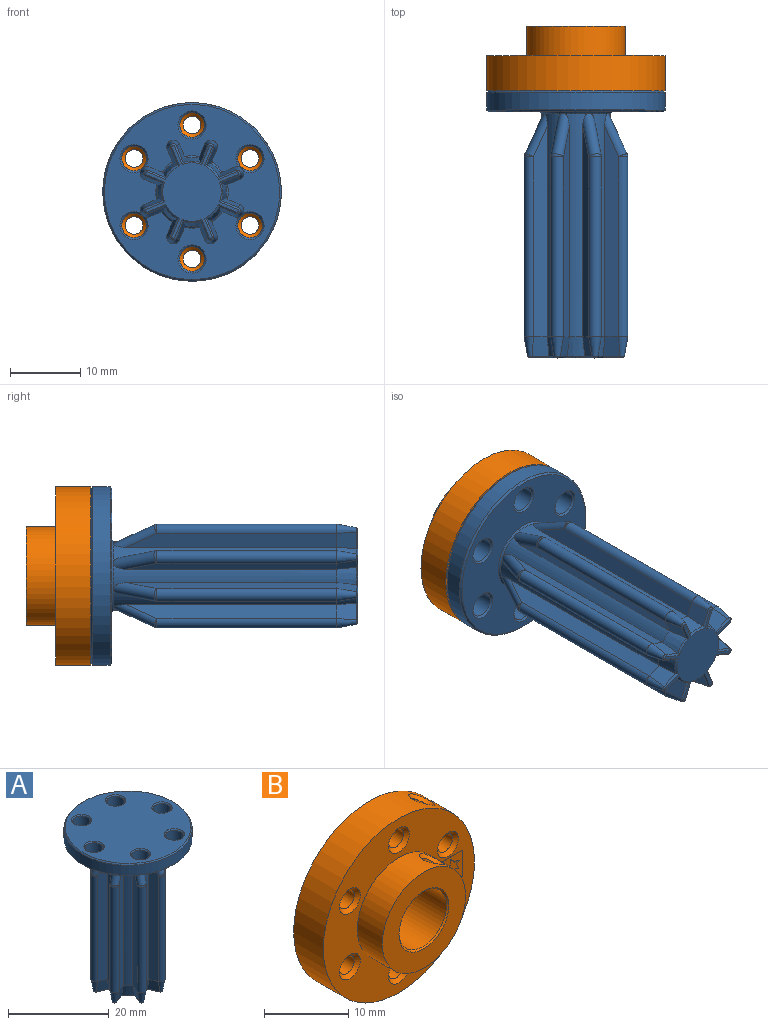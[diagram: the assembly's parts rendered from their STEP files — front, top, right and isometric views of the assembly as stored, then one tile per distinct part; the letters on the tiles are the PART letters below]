
ASSEMBLY  parts=2 mates=1
PART A: 137 faces, bbox 25.4x25.4x38 mm
  f0: cylinder r=4.9mm len=31.75mm, axis (0,0,1), area 62.1mm2, adj f20,f23,f45,f74,f76,f129
  f1: cylinder r=4.9mm len=31.75mm, axis (0,0,1), area 62.1mm2, adj f17,f19,f37,f76,f78,f129
  f2: cylinder r=4.9mm len=31.75mm, axis (0,0,1), area 62.1mm2, adj f14,f16,f36,f78,f81,f129
  f3: cylinder r=4.9mm len=31.75mm, axis (0,0,1), area 62.1mm2, adj f13,f30,f44,f81,f82,f129
  f4: cylinder r=4.9mm len=31.75mm, axis (0,0,1), area 62.1mm2, adj f29,f31,f52,f82,f84,f129
  f5: cylinder r=4.9mm len=31.75mm, axis (0,0,1), area 62.1mm2, adj f25,f28,f60,f84,f86,f129
  f6: cylinder r=4.9mm len=31.75mm, axis (0,0,1), area 62.1mm2, adj f8,f26,f61,f86,f88,f129
  f7: cylinder r=4.9mm len=31.75mm, axis (0,0,1), area 62.1mm2, adj f9,f22,f53,f74,f88,f129
  f8: plane 29.88x1.98mm, normal (0.38,-0.92,0), area 59.4mm2, adj f6,f10,f59,f88
  f9: plane 29.88x1.98mm, normal (-0.38,0.92,0), area 59.4mm2, adj f7,f10,f55,f88
  f10: cylinder r=0.95mm len=25.59mm, axis (0,0,1), area 76.4mm2, adj f8,f9,f57,f89
  f11: plane 13.26x13.26mm, normal (0,0,-1), area 64.4mm2, adj f90,f91,f92,f93,f94,f95,f96,f97
  f12: cylinder r=0.95mm len=25.59mm, axis (0,0,1), area 76.4mm2, adj f13,f14,f40,f80
  f13: plane 29.88x1.98mm, normal (0.38,-0.92,0), area 59.4mm2, adj f3,f12,f42,f81
  f14: plane 29.88x1.98mm, normal (-0.38,0.92,0), area 59.4mm2, adj f2,f12,f38,f81
  f15: cylinder r=0.95mm len=25.59mm, axis (0,0,1), area 76.4mm2, adj f16,f17,f33,f79
  f16: plane 29.88x1.98mm, normal (0.92,-0.38,0), area 59.4mm2, adj f2,f15,f34,f78
  f17: plane 29.88x1.98mm, normal (-0.92,0.38,0), area 59.4mm2, adj f1,f15,f35,f78
  f18: cylinder r=0.95mm len=25.59mm, axis (0,0,1), area 76.4mm2, adj f19,f20,f41,f77
  f19: plane 29.88x1.98mm, normal (0.92,0.38,0), area 59.4mm2, adj f1,f18,f39,f76
  f20: plane 29.88x1.98mm, normal (-0.92,-0.38,0), area 59.4mm2, adj f0,f18,f43,f76
  f21: cylinder r=0.95mm len=25.59mm, axis (0,0,1), area 76.4mm2, adj f22,f23,f49,f75
  f22: plane 29.88x1.98mm, normal (-0.38,-0.92,0), area 59.4mm2, adj f7,f21,f51,f74
  f23: plane 29.88x1.98mm, normal (0.38,0.92,0), area 59.4mm2, adj f0,f21,f47,f74
  f24: cylinder r=0.95mm len=25.59mm, axis (0,0,1), area 76.4mm2, adj f25,f26,f64,f87
  f25: plane 29.88x1.98mm, normal (0.92,-0.38,0), area 59.4mm2, adj f5,f24,f62,f86
  f26: plane 29.88x1.98mm, normal (-0.92,0.38,0), area 59.4mm2, adj f6,f24,f63,f86
  f27: cylinder r=0.95mm len=25.59mm, axis (0,0,1), area 76.4mm2, adj f28,f29,f56,f85
  f28: plane 29.88x1.98mm, normal (-0.92,-0.38,0), area 59.4mm2, adj f5,f27,f58,f84
  f29: plane 29.88x1.98mm, normal (0.92,0.38,0), area 59.4mm2, adj f4,f27,f54,f84
  f30: plane 29.88x1.98mm, normal (0.38,0.92,0), area 59.4mm2, adj f3,f32,f46,f82
  f31: plane 29.88x1.98mm, normal (-0.38,-0.92,0), area 59.4mm2, adj f4,f32,f50,f82
  f32: cylinder r=0.95mm len=25.59mm, axis (0,0,1), area 76.4mm2, adj f30,f31,f48,f83
  f33: cone r=0.42mm half-angle=10deg, axis (0,0,1), area 6.3mm2, adj f15,f34,f35,f110
  f34: plane 2.81x2.39mm, normal (0.91,-0.38,-0.17), area 6.7mm2, adj f16,f33,f36,f108
  f35: plane 2.81x2.58mm, normal (-0.91,0.38,-0.17), area 6.7mm2, adj f17,f33,f37,f112
  f36: cone r=4.37mm half-angle=10deg, axis (0,0,1), area 6.4mm2, adj f2,f34,f38,f106
  f37: cone r=4.37mm half-angle=10deg, axis (0,0,1), area 6.4mm2, adj f1,f35,f39,f114
  f38: plane 2.81x2.39mm, normal (-0.38,0.91,-0.17), area 6.7mm2, adj f14,f36,f40,f104
  f39: plane 2.81x2.58mm, normal (0.91,0.38,-0.17), area 6.7mm2, adj f19,f37,f41,f116
  f40: cone r=0.42mm half-angle=10deg, axis (0,0,1), area 6.3mm2, adj f12,f38,f42,f102
  f41: cone r=0.42mm half-angle=10deg, axis (0,0,1), area 6.3mm2, adj f18,f39,f43,f118
  f42: plane 2.81x2.58mm, normal (0.38,-0.91,-0.17), area 6.7mm2, adj f13,f40,f44,f100
  f43: plane 2.81x2.39mm, normal (-0.91,-0.38,-0.17), area 6.7mm2, adj f20,f41,f45,f120
  f44: cone r=4.37mm half-angle=10deg, axis (0,0,1), area 6.4mm2, adj f3,f42,f46,f98
  f45: cone r=4.37mm half-angle=10deg, axis (0,0,1), area 6.4mm2, adj f0,f43,f47,f121
  f46: plane 2.81x2.58mm, normal (0.38,0.91,-0.17), area 6.7mm2, adj f30,f44,f48,f96
  f47: plane 2.81x2.39mm, normal (0.38,0.91,-0.17), area 6.7mm2, adj f23,f45,f49,f119
  f48: cone r=0.42mm half-angle=10deg, axis (0,0,1), area 6.3mm2, adj f32,f46,f50,f94
  f49: cone r=0.42mm half-angle=10deg, axis (0,0,1), area 6.3mm2, adj f21,f47,f51,f117
  f50: plane 2.81x2.39mm, normal (-0.38,-0.91,-0.17), area 6.7mm2, adj f31,f48,f52,f92
  f51: plane 2.81x2.58mm, normal (-0.38,-0.91,-0.17), area 6.7mm2, adj f22,f49,f53,f115
  f52: cone r=4.37mm half-angle=10deg, axis (0,0,1), area 6.4mm2, adj f4,f50,f54,f90
  f53: cone r=4.37mm half-angle=10deg, axis (0,0,1), area 6.4mm2, adj f7,f51,f55,f113
  f54: plane 2.81x2.39mm, normal (0.91,0.38,-0.17), area 6.7mm2, adj f29,f52,f56,f91
  f55: plane 2.81x2.58mm, normal (-0.38,0.91,-0.17), area 6.7mm2, adj f9,f53,f57,f111
  f56: cone r=0.42mm half-angle=10deg, axis (0,0,1), area 6.3mm2, adj f27,f54,f58,f93
  f57: cone r=0.42mm half-angle=10deg, axis (0,0,1), area 6.3mm2, adj f10,f55,f59,f109
  f58: plane 2.81x2.58mm, normal (-0.91,-0.38,-0.17), area 6.7mm2, adj f28,f56,f60,f95
  f59: plane 2.81x2.39mm, normal (0.38,-0.91,-0.17), area 6.7mm2, adj f8,f57,f61,f107
  f60: cone r=4.37mm half-angle=10deg, axis (0,0,1), area 6.4mm2, adj f5,f58,f62,f97
  f61: cone r=4.37mm half-angle=10deg, axis (0,0,1), area 6.4mm2, adj f6,f59,f63,f105
  f62: plane 2.81x2.58mm, normal (0.91,-0.38,-0.17), area 6.7mm2, adj f25,f60,f64,f99
  f63: plane 2.81x2.39mm, normal (-0.91,0.38,-0.17), area 6.7mm2, adj f26,f61,f64,f103
  f64: cone r=0.42mm half-angle=10deg, axis (0,0,1), area 6.3mm2, adj f24,f62,f63,f101
  f65: cylinder r=1.75mm len=3.5mm, axis (0,0,-1), area 27.5mm2, adj f127,f135
  f66: cylinder r=1.75mm len=3.5mm, axis (0,0,-1), area 27.5mm2, adj f126,f134
  f67: cylinder r=1.75mm len=3.5mm, axis (0,0,-1), area 27.5mm2, adj f125,f133
  f68: cylinder r=1.75mm len=3.5mm, axis (0,0,-1), area 27.5mm2, adj f124,f132
  f69: cylinder r=1.75mm len=3.5mm, axis (0,0,-1), area 27.5mm2, adj f123,f131
  f70: cylinder r=1.75mm len=3.5mm, axis (0,0,-1), area 27.5mm2, adj f122,f130
  f71: cylinder r=12.7mm len=25.4mm, axis (0,0,-1), area 199.5mm2, adj f128,f136
  f72: plane 24.9x24.9mm, normal (0,0,1), area 411.6mm2, adj f122,f123,f124,f125,f126,f127,f128
  f73: plane 24.9x24.9mm, normal (0,0,-1), area 328.2mm2, adj f129,f130,f131,f132,f133,f134,f135,f136
  f74: cylinder r=0.95mm len=6.18mm, axis (0.41,-0.17,0.89), area 17.6mm2, adj f0,f7,f22,f23,f75,f129
  f75: sphere r=0.95mm, area 0.8mm2, adj f21,f74
  f76: cylinder r=0.95mm len=6.18mm, axis (0.17,-0.41,0.89), area 17.6mm2, adj f0,f1,f19,f20,f77,f129
  f77: sphere r=0.95mm, area 0.8mm2, adj f18,f76
  f78: cylinder r=0.95mm len=6.18mm, axis (-0.17,-0.41,0.89), area 17.6mm2, adj f1,f2,f16,f17,f79,f129
  f79: sphere r=0.95mm, area 0.8mm2, adj f15,f78
  f80: sphere r=0.95mm, area 0.8mm2, adj f12,f81
  f81: cylinder r=0.95mm len=6.18mm, axis (0.41,0.17,-0.89), area 17.6mm2, adj f2,f3,f13,f14,f80,f129
  f82: cylinder r=0.95mm len=6.18mm, axis (-0.41,0.17,0.89), area 17.6mm2, adj f3,f4,f30,f31,f83,f129
  f83: sphere r=0.95mm, area 0.8mm2, adj f32,f82
  f84: cylinder r=0.95mm len=6.18mm, axis (-0.17,0.41,0.89), area 17.6mm2, adj f4,f5,f28,f29,f85,f129
  f85: sphere r=0.95mm, area 0.8mm2, adj f27,f84
  f86: cylinder r=0.95mm len=6.18mm, axis (0.17,0.41,0.89), area 17.6mm2, adj f5,f6,f25,f26,f87,f129
  f87: sphere r=0.95mm, area 0.8mm2, adj f24,f86
  f88: cylinder r=0.95mm len=6.18mm, axis (0.41,0.17,0.89), area 17.6mm2, adj f6,f7,f8,f9,f89,f129
  f89: sphere r=0.95mm, area 0.8mm2, adj f10,f88
  f90: cone r=4.16mm half-angle=50deg, axis (0,0,1), area 0.9mm2, adj f11,f52,f91,f92
  f91: plane 2.59x1.3mm, normal (0.59,0.25,-0.77), area 0.9mm2, adj f11,f54,f90,f93
  f92: plane 2.59x1.3mm, normal (-0.25,-0.59,-0.77), area 0.9mm2, adj f11,f50,f90,f94
  f93: cone r=0.21mm half-angle=50deg, axis (0,0,1), area 0.3mm2, adj f11,f56,f91,f95
  f94: cone r=0.21mm half-angle=50deg, axis (0,0,1), area 0.3mm2, adj f11,f48,f92,f96
  f95: plane 2.68x1.22mm, normal (-0.59,-0.25,-0.77), area 0.9mm2, adj f11,f58,f93,f97
  f96: plane 2.68x1.22mm, normal (0.25,0.59,-0.77), area 0.9mm2, adj f11,f46,f94,f98
  f97: cone r=4.16mm half-angle=50deg, axis (0,0,1), area 0.9mm2, adj f11,f60,f95,f99
  f98: cone r=4.16mm half-angle=50deg, axis (0,0,1), area 0.9mm2, adj f11,f44,f96,f100
  f99: plane 2.68x1.22mm, normal (0.59,-0.25,-0.77), area 0.9mm2, adj f11,f62,f97,f101
  f100: plane 2.68x1.22mm, normal (0.25,-0.59,-0.77), area 0.9mm2, adj f11,f42,f98,f102
  f101: cone r=0.21mm half-angle=50deg, axis (0,0,1), area 0.3mm2, adj f11,f64,f99,f103
  f102: cone r=0.21mm half-angle=50deg, axis (0,0,1), area 0.3mm2, adj f11,f40,f100,f104
  f103: plane 2.59x1.3mm, normal (-0.59,0.25,-0.77), area 0.9mm2, adj f11,f63,f101,f105
  f104: plane 2.59x1.3mm, normal (-0.25,0.59,-0.77), area 0.9mm2, adj f11,f38,f102,f106
  f105: cone r=4.16mm half-angle=50deg, axis (0,0,1), area 0.9mm2, adj f11,f61,f103,f107
  f106: cone r=4.16mm half-angle=50deg, axis (0,0,1), area 0.9mm2, adj f11,f36,f104,f108
  f107: plane 2.59x1.3mm, normal (0.25,-0.59,-0.77), area 0.9mm2, adj f11,f59,f105,f109
  f108: plane 2.59x1.3mm, normal (0.59,-0.25,-0.77), area 0.9mm2, adj f11,f34,f106,f110
  f109: cone r=0.21mm half-angle=50deg, axis (0,0,1), area 0.3mm2, adj f11,f57,f107,f111
  f110: cone r=0.21mm half-angle=50deg, axis (0,0,1), area 0.3mm2, adj f11,f33,f108,f112
  f111: plane 2.68x1.22mm, normal (-0.25,0.59,-0.77), area 0.9mm2, adj f11,f55,f109,f113
  f112: plane 2.68x1.22mm, normal (-0.59,0.25,-0.77), area 0.9mm2, adj f11,f35,f110,f114
  f113: cone r=4.16mm half-angle=50deg, axis (0,0,1), area 0.9mm2, adj f11,f53,f111,f115
  f114: cone r=4.16mm half-angle=50deg, axis (0,0,1), area 0.9mm2, adj f11,f37,f112,f116
  f115: plane 2.68x1.22mm, normal (-0.25,-0.59,-0.77), area 0.9mm2, adj f11,f51,f113,f117
  f116: plane 2.68x1.22mm, normal (0.59,0.25,-0.77), area 0.9mm2, adj f11,f39,f114,f118
  f117: cone r=0.21mm half-angle=50deg, axis (0,0,1), area 0.3mm2, adj f11,f49,f115,f119
  f118: cone r=0.21mm half-angle=50deg, axis (0,0,1), area 0.3mm2, adj f11,f41,f116,f120
  f119: plane 2.59x1.3mm, normal (0.25,0.59,-0.77), area 0.9mm2, adj f11,f47,f117,f121
  f120: plane 2.59x1.3mm, normal (-0.59,-0.25,-0.77), area 0.9mm2, adj f11,f43,f118,f121
  f121: cone r=4.16mm half-angle=50deg, axis (0,0,1), area 0.9mm2, adj f11,f45,f119,f120
  f122: cone r=1.75mm half-angle=45deg, axis (0,0,1), area 4.2mm2, adj f70,f72
  f123: cone r=1.75mm half-angle=45deg, axis (0,0,1), area 4.2mm2, adj f69,f72
  f124: cone r=1.75mm half-angle=45deg, axis (0,0,1), area 4.2mm2, adj f68,f72
  f125: cone r=1.75mm half-angle=45deg, axis (0,0,1), area 4.2mm2, adj f67,f72
  f126: cone r=1.75mm half-angle=45deg, axis (0,0,1), area 4.2mm2, adj f66,f72
  f127: cone r=1.75mm half-angle=45deg, axis (0,0,1), area 4.2mm2, adj f65,f72
  f128: cone r=12.45mm half-angle=45deg, axis (0,0,-1), area 27.9mm2, adj f71,f72
  f129: cone r=5.15mm half-angle=45deg, axis (0,0,1), area 11.2mm2, adj f0,f1,f2,f3,f4,f5,f6,f7
  f130: cone r=2mm half-angle=45deg, axis (0,0,-1), area 4.2mm2, adj f70,f73
  f131: cone r=2mm half-angle=45deg, axis (0,0,-1), area 4.2mm2, adj f69,f73
  f132: cone r=2mm half-angle=45deg, axis (0,0,-1), area 4.2mm2, adj f68,f73
  f133: cone r=2mm half-angle=45deg, axis (0,0,-1), area 4.2mm2, adj f67,f73
  f134: cone r=2mm half-angle=45deg, axis (0,0,-1), area 4.2mm2, adj f66,f73
  f135: cone r=2mm half-angle=45deg, axis (0,0,-1), area 4.2mm2, adj f65,f73
  f136: cone r=12.7mm half-angle=45deg, axis (0,0,1), area 27.9mm2, adj f71,f73
PART B: 277 faces, bbox 25.4x9.2x25.4 mm
  f0: bspline ~3.27x2.94mm, area 5.6mm2, adj f17,f26
  f1: bspline ~3.12x2.88mm, area 5mm2, adj f16,f19
  f2: cone r=4mm half-angle=45deg, axis (0,-1,0), area 7.3mm2, adj f18,f29
  f3: cone r=4.2mm half-angle=45deg, axis (0,1,0), area 7.3mm2, adj f18,f28
  f4: cone r=1.25mm half-angle=45deg, axis (0,-1,0), area 6.7mm2, adj f25,f27
  f5: cone r=1.25mm half-angle=45deg, axis (0,-1,0), area 6.7mm2, adj f24,f27
  f6: cone r=1.25mm half-angle=45deg, axis (0,-1,0), area 6.7mm2, adj f23,f27
  f7: cone r=1.25mm half-angle=45deg, axis (0,-1,0), area 6.7mm2, adj f22,f27
  f8: cone r=1.25mm half-angle=45deg, axis (0,-1,0), area 6.7mm2, adj f21,f27
  f9: cone r=1.25mm half-angle=45deg, axis (0,-1,0), area 6.7mm2, adj f20,f27
  f10: cone r=1.75mm half-angle=45deg, axis (0,1,0), area 6.7mm2, adj f20,f28
  f11: cone r=1.75mm half-angle=45deg, axis (0,1,0), area 6.7mm2, adj f25,f28
  f12: cone r=1.75mm half-angle=45deg, axis (0,1,0), area 6.7mm2, adj f24,f28
  f13: cone r=1.75mm half-angle=45deg, axis (0,1,0), area 6.7mm2, adj f23,f28
  f14: cone r=1.75mm half-angle=45deg, axis (0,1,0), area 6.7mm2, adj f22,f28
  f15: cone r=1.75mm half-angle=45deg, axis (0,1,0), area 6.7mm2, adj f21,f28
  f16: cylinder r=1.25mm len=3.65mm, axis (0.5,0,0.87), area 20.3mm2, adj f1,f18
  f17: cylinder r=1.25mm len=8.57mm, axis (0.5,0,0.87), area 65.1mm2, adj f0,f18
  f18: cylinder r=4mm len=8.8mm, axis (0,-1,0), area 211.2mm2, adj f2,f3,f16,f17
  f19: cylinder r=7mm len=14mm, axis (0,1,0), area 176.5mm2, adj f1,f27,f29
  f20: cylinder r=1.25mm len=4mm, axis (0,-1,0), area 31.4mm2, adj f9,f10
  f21: cylinder r=1.25mm len=4mm, axis (0,-1,0), area 31.4mm2, adj f8,f15
  f22: cylinder r=1.25mm len=4mm, axis (0,-1,0), area 31.4mm2, adj f7,f14
  f23: cylinder r=1.25mm len=4mm, axis (0,-1,0), area 31.4mm2, adj f6,f13
  f24: cylinder r=1.25mm len=4mm, axis (0,-1,0), area 31.4mm2, adj f5,f12
  f25: cylinder r=1.25mm len=4mm, axis (0,-1,0), area 31.4mm2, adj f4,f11
  f26: cylinder r=12.7mm len=25.4mm, axis (0,1,0), area 390.2mm2, adj f0,f27,f28
  f27: plane 25.4x25.4mm, normal (0,-1,0), area 282.8mm2, adj f4,f5,f6,f7,f8,f9,f19,f26
  f28: plane 25.4x25.4mm, normal (0,1,0), area 393.6mm2, adj f3,f10,f11,f12,f13,f14,f15,f26
  f29: plane 14x14mm, normal (0,-1,0), area 98.5mm2, adj f2,f19
  f30: plane 0.05x0.04mm, normal (0,0,-1), area 0mm2, adj f27,f31,f42,f43
  f31: plane 0.24x0.06mm, normal (-0.97,0,0.25), area 0mm2, adj f27,f30,f32,f43
  f32: plane 0.05x0.04mm, normal (0,0,1), area 0mm2, adj f27,f31,f33,f43
  f33: plane 0.19x0.06mm, normal (0.95,0,0.31), area 0mm2, adj f27,f32,f34,f43
  f34: plane 0.19x0.06mm, normal (-0.95,0,0.31), area 0mm2, adj f27,f33,f35,f43
  f35: plane 0.05x0.04mm, normal (0,0,1), area 0mm2, adj f27,f34,f36,f43
  f36: plane 0.24x0.06mm, normal (0.97,0,0.25), area 0mm2, adj f27,f35,f37,f43
  f37: plane 0.05x0.04mm, normal (0,0,-1), area 0mm2, adj f27,f36,f38,f43
  f38: plane 0.19x0.05mm, normal (-0.97,0,-0.23), area 0mm2, adj f27,f37,f39,f43
  f39: plane 0.19x0.06mm, normal (0.95,0,-0.31), area 0mm2, adj f27,f38,f40,f43
  f40: plane 0.05x0.03mm, normal (0,0,-1), area 0mm2, adj f27,f39,f41,f43
  f41: plane 0.19x0.06mm, normal (-0.95,0,-0.31), area 0mm2, adj f27,f40,f42,f43
  f42: plane 0.19x0.05mm, normal (0.98,0,-0.21), area 0mm2, adj f27,f30,f41,f43
  f43: plane 0.32x0.24mm, normal (0,-1,0), area 0mm2, adj f30,f31,f32,f33,f34,f35,f36,f37
  f44: extruded ~0.13x0.11mm, area 0mm2, adj f27,f45,f47,f48
  f45: extruded ~0.13x0.11mm, area 0mm2, adj f27,f44,f46,f48
  f46: extruded ~0.13x0.11mm, area 0mm2, adj f27,f45,f47,f48
  f47: extruded ~0.13x0.11mm, area 0mm2, adj f27,f44,f46,f48
  f48: plane 0.26x0.22mm, normal (0,-1,0), area 0mm2, adj f44,f45,f46,f47,f49,f50,f51,f52
  f49: extruded ~0.09x0.07mm, area 0mm2, adj f48,f50,f52,f270
  f50: extruded ~0.09x0.07mm, area 0mm2, adj f48,f49,f51,f270
  f51: extruded ~0.09x0.07mm, area 0mm2, adj f48,f50,f52,f270
  f52: extruded ~0.09x0.07mm, area 0mm2, adj f48,f49,f51,f270
  f53: plane 0.34x0.05mm, normal (-1,0,0), area 0mm2, adj f27,f54,f56,f57
  f54: plane 0.05x0.04mm, normal (0,0,1), area 0mm2, adj f27,f53,f55,f57
  f55: plane 0.34x0.05mm, normal (1,0,0), area 0mm2, adj f27,f54,f56,f57
  f56: plane 0.05x0.04mm, normal (0,0,-1), area 0mm2, adj f27,f53,f55,f57
  f57: plane 0.34x0.04mm, normal (0,-1,0), area 0mm2, adj f53,f54,f55,f56
  f58: plane 0.06x0.05mm, normal (-1,0,0), area 0mm2, adj f27,f59,f61,f62
  f59: plane 0.05x0.05mm, normal (0,0,1), area 0mm2, adj f27,f58,f60,f62
  f60: plane 0.06x0.05mm, normal (1,0,0), area 0mm2, adj f27,f59,f61,f62
  f61: plane 0.05x0.05mm, normal (0,0,-1), area 0mm2, adj f27,f58,f60,f62
  f62: plane 0.06x0.05mm, normal (0,-1,0), area 0mm2, adj f58,f59,f60,f61
  f63: plane 0.24x0.05mm, normal (-1,0,0), area 0mm2, adj f27,f64,f75,f76
  f64: plane 0.05x0.04mm, normal (0,0,1), area 0mm2, adj f27,f63,f65,f76
  f65: plane 0.05x0.03mm, normal (1,0,0), area 0mm2, adj f27,f64,f66,f76
  f66: extruded ~0.08x0.05mm, area 0mm2, adj f27,f65,f67,f76
  f67: extruded ~0.09x0.08mm, area 0mm2, adj f27,f66,f68,f76
  f68: plane 0.16x0.05mm, normal (1,0,0), area 0mm2, adj f27,f67,f69,f76
  f69: plane 0.05x0.04mm, normal (0,0,-1), area 0mm2, adj f27,f68,f70,f76
  f70: plane 0.14x0.05mm, normal (-1,0,0), area 0mm2, adj f27,f69,f71,f76
  f71: extruded ~0.06x0.05mm, area 0mm2, adj f27,f70,f72,f76
  f72: extruded ~0.05x0.04mm, area 0mm2, adj f27,f71,f73,f76
  f73: extruded ~0.07x0.05mm, area 0mm2, adj f27,f72,f74,f76
  f74: plane 0.18x0.05mm, normal (1,0,0), area 0mm2, adj f27,f73,f75,f76
  f75: plane 0.05x0.04mm, normal (0,0,-1), area 0mm2, adj f27,f63,f74,f76
  f76: plane 0.25x0.2mm, normal (0,-1,0), area 0mm2, adj f63,f64,f65,f66,f67,f68,f69,f70
  f77: plane 0.34x0.05mm, normal (-1,0,0), area 0mm2, adj f27,f78,f80,f81
  f78: plane 0.05x0.04mm, normal (0,0,1), area 0mm2, adj f27,f77,f79,f81
  f79: plane 0.34x0.05mm, normal (1,0,0), area 0mm2, adj f27,f78,f80,f81
  f80: plane 0.05x0.04mm, normal (0,0,-1), area 0mm2, adj f27,f77,f79,f81
  f81: plane 0.34x0.04mm, normal (0,-1,0), area 0mm2, adj f77,f78,f79,f80
  f82: plane 0.06x0.05mm, normal (-1,0,0), area 0mm2, adj f27,f83,f85,f86
  f83: plane 0.05x0.05mm, normal (0,0,1), area 0mm2, adj f27,f82,f84,f86
  f84: plane 0.06x0.05mm, normal (1,0,0), area 0mm2, adj f27,f83,f85,f86
  f85: plane 0.05x0.05mm, normal (0,0,-1), area 0mm2, adj f27,f82,f84,f86
  f86: plane 0.06x0.05mm, normal (0,-1,0), area 0mm2, adj f82,f83,f84,f85
  f87: extruded ~0.13x0.11mm, area 0mm2, adj f27,f88,f90,f91
  f88: extruded ~0.13x0.11mm, area 0mm2, adj f27,f87,f89,f91
  f89: extruded ~0.13x0.11mm, area 0mm2, adj f27,f88,f90,f91
  f90: extruded ~0.13x0.11mm, area 0mm2, adj f27,f87,f89,f91
  f91: plane 0.26x0.22mm, normal (0,-1,0), area 0mm2, adj f87,f88,f89,f90,f92,f93,f94,f95
  f92: extruded ~0.09x0.07mm, area 0mm2, adj f91,f93,f95,f271
  f93: extruded ~0.09x0.07mm, area 0mm2, adj f91,f92,f94,f271
  f94: extruded ~0.09x0.07mm, area 0mm2, adj f91,f93,f95,f271
  f95: extruded ~0.09x0.07mm, area 0mm2, adj f91,f92,f94,f271
  f96: extruded ~0.13x0.09mm, area 0mm2, adj f27,f97,f105,f106
  f97: extruded ~0.1x0.05mm, area 0mm2, adj f27,f96,f98,f106
  f98: cylinder r=0.1mm len=0.07mm, axis (0,1,0), area 0mm2, adj f27,f97,f99,f106
  f99: cylinder r=0.12mm len=0.06mm, axis (0,1,0), area 0mm2, adj f27,f98,f100,f106
  f100: plane 0.1x0.05mm, normal (-1,0,0), area 0mm2, adj f27,f99,f101,f106
  f101: plane 0.05x0.04mm, normal (0,0,1), area 0mm2, adj f27,f100,f102,f106
  f102: plane 0.33x0.05mm, normal (1,0,0), area 0mm2, adj f27,f101,f103,f106
  f103: plane 0.05x0.04mm, normal (0,0,-1), area 0mm2, adj f27,f102,f104,f106
  f104: plane 0.05x0.02mm, normal (-1,0,0), area 0mm2, adj f27,f103,f105,f106
  f105: extruded ~0.08x0.05mm, area 0mm2, adj f27,f96,f104,f106
  f106: plane 0.34x0.21mm, normal (0,-1,0), area 0mm2, adj f96,f97,f98,f99,f100,f101,f102,f103
  f107: extruded ~0.09x0.07mm, area 0mm2, adj f106,f108,f111,f272
  f108: extruded ~0.06x0.05mm, area 0mm2, adj f106,f107,f109,f272
  f109: plane 0.14x0.05mm, normal (-1,0,0), area 0mm2, adj f106,f108,f110,f272
  f110: extruded ~0.07x0.05mm, area 0mm2, adj f106,f109,f111,f272
  f111: extruded ~0.09x0.06mm, area 0mm2, adj f106,f107,f110,f272
  f112: plane 0.05x0.04mm, normal (0,0,-1), area 0mm2, adj f27,f113,f124,f125
  f113: plane 0.24x0.06mm, normal (-0.97,0,0.25), area 0mm2, adj f27,f112,f114,f125
  f114: plane 0.05x0.04mm, normal (0,0,1), area 0mm2, adj f27,f113,f115,f125
  f115: plane 0.19x0.06mm, normal (0.95,0,0.31), area 0mm2, adj f27,f114,f116,f125
  f116: plane 0.19x0.06mm, normal (-0.95,0,0.31), area 0mm2, adj f27,f115,f117,f125
  f117: plane 0.05x0.04mm, normal (0,0,1), area 0mm2, adj f27,f116,f118,f125
  f118: plane 0.24x0.06mm, normal (0.97,0,0.25), area 0mm2, adj f27,f117,f119,f125
  f119: plane 0.05x0.04mm, normal (0,0,-1), area 0mm2, adj f27,f118,f120,f125
  f120: plane 0.19x0.05mm, normal (-0.97,0,-0.23), area 0mm2, adj f27,f119,f121,f125
  f121: plane 0.19x0.06mm, normal (0.95,0,-0.31), area 0mm2, adj f27,f120,f122,f125
  f122: plane 0.05x0.03mm, normal (0,0,-1), area 0mm2, adj f27,f121,f123,f125
  f123: plane 0.19x0.06mm, normal (-0.95,0,-0.31), area 0mm2, adj f27,f122,f124,f125
  f124: plane 0.19x0.05mm, normal (0.98,0,-0.21), area 0mm2, adj f27,f112,f123,f125
  f125: plane 0.32x0.24mm, normal (0,-1,0), area 0mm2, adj f112,f113,f114,f115,f116,f117,f118,f119
  f126: plane 0.05x0.04mm, normal (0,0,-1), area 0mm2, adj f27,f127,f138,f139
  f127: plane 0.24x0.06mm, normal (-0.97,0,0.25), area 0mm2, adj f27,f126,f128,f139
  f128: plane 0.05x0.04mm, normal (0,0,1), area 0mm2, adj f27,f127,f129,f139
  f129: plane 0.19x0.06mm, normal (0.95,0,0.31), area 0mm2, adj f27,f128,f130,f139
  f130: plane 0.19x0.06mm, normal (-0.95,0,0.31), area 0mm2, adj f27,f129,f131,f139
  f131: plane 0.05x0.04mm, normal (0,0,1), area 0mm2, adj f27,f130,f132,f139
  f132: plane 0.24x0.06mm, normal (0.97,0,0.25), area 0mm2, adj f27,f131,f133,f139
  f133: plane 0.05x0.04mm, normal (0,0,-1), area 0mm2, adj f27,f132,f134,f139
  f134: plane 0.19x0.05mm, normal (-0.97,0,-0.23), area 0mm2, adj f27,f133,f135,f139
  f135: plane 0.19x0.06mm, normal (0.95,0,-0.31), area 0mm2, adj f27,f134,f136,f139
  f136: plane 0.05x0.03mm, normal (0,0,-1), area 0mm2, adj f27,f135,f137,f139
  f137: plane 0.19x0.06mm, normal (-0.95,0,-0.31), area 0mm2, adj f27,f136,f138,f139
  f138: plane 0.19x0.05mm, normal (0.98,0,-0.21), area 0mm2, adj f27,f126,f137,f139
  f139: plane 0.32x0.24mm, normal (0,-1,0), area 0mm2, adj f126,f127,f128,f129,f130,f131,f132,f133
  f140: extruded ~0.33x0.32mm, area 0mm2, adj f27,f141,f145,f146
  f141: plane 0.05x0mm, normal (1,0,0), area 0mm2, adj f27,f140,f142,f146
  f142: extruded ~0.33x0.32mm, area 0mm2, adj f27,f141,f143,f146
  f143: extruded ~0.33x0.32mm, area 0mm2, adj f27,f142,f144,f146
  f144: plane 0.05x0mm, normal (-1,0,0), area 0mm2, adj f27,f143,f145,f146
  f145: extruded ~0.33x0.32mm, area 0mm2, adj f27,f140,f144,f146
  f146: plane 0.66x0.64mm, normal (0,-1,0), area 0.3mm2, adj f140,f141,f142,f143,f144,f145,f147,f148
  f147: extruded ~0.15x0.14mm, area 0mm2, adj f146,f148,f152,f273
  f148: extruded ~0.15x0.14mm, area 0mm2, adj f146,f147,f149,f273
  f149: plane 0.05x0mm, normal (-1,0,0), area 0mm2, adj f146,f148,f150,f273
  f150: extruded ~0.15x0.14mm, area 0mm2, adj f146,f149,f151,f273
  f151: extruded ~0.15x0.14mm, area 0mm2, adj f146,f150,f152,f273
  f152: plane 0.05x0mm, normal (1,0,0), area 0mm2, adj f146,f147,f151,f273
  f153: plane 0.97x0.05mm, normal (1,0,0), area 0mm2, adj f27,f154,f156,f157
  f154: plane 0.2x0.05mm, normal (0,0,-1), area 0mm2, adj f27,f153,f155,f157
  f155: plane 0.97x0.05mm, normal (-1,0,0), area 0mm2, adj f27,f154,f156,f157
  f156: plane 0.2x0.05mm, normal (0,0,1), area 0mm2, adj f27,f153,f155,f157
  f157: plane 0.97x0.2mm, normal (0,-1,0), area 0.2mm2, adj f153,f154,f155,f156
  f158: extruded ~0.63x0.35mm, area 0mm2, adj f27,f159,f177,f178
  f159: extruded ~1.4x0.15mm, area 0.1mm2, adj f27,f158,f160,f178
  f160: sphere r=1.94mm, area 0mm2, adj f27,f159,f161,f178
  f161: extruded ~0.66x0.34mm, area 0mm2, adj f27,f160,f162,f178
  f162: extruded ~0.59x0.38mm, area 0mm2, adj f27,f161,f163,f178
  f163: extruded ~0.88x0.17mm, area 0mm2, adj f27,f162,f164,f178
  f164: extruded ~0.64x0.64mm, area 0mm2, adj f27,f163,f165,f178
  f165: extruded ~0.75x0.1mm, area 0mm2, adj f27,f164,f166,f178
  f166: extruded ~0.8x0.35mm, area 0mm2, adj f27,f165,f167,f178
  f167: extruded ~0.67x0.22mm, area 0mm2, adj f27,f166,f168,f178
  f168: extruded ~0.73x0.17mm, area 0mm2, adj f27,f167,f169,f178
  f169: extruded ~0.68x0.4mm, area 0mm2, adj f27,f168,f170,f178
  f170: extruded ~1.41x0.18mm, area 0.1mm2, adj f27,f169,f171,f178
  f171: extruded ~0.41x0.1mm, area 0mm2, adj f27,f170,f172,f178
  f172: extruded ~0.39x0.23mm, area 0mm2, adj f27,f171,f173,f178
  f173: plane 0.77x0.05mm, normal (0,0,1), area 0mm2, adj f27,f172,f174,f178
  f174: plane 3.81x0.05mm, normal (1,0,0), area 0.2mm2, adj f27,f173,f175,f178
  f175: plane 3.46x0.05mm, normal (0,0,-1), area 0.2mm2, adj f27,f174,f176,f178
  f176: plane 3.81x0.05mm, normal (-1,0,0), area 0.2mm2, adj f27,f175,f177,f178
  f177: plane 0.68x0.05mm, normal (0,0,1), area 0mm2, adj f27,f158,f176,f178
  f178: plane 3.81x3.46mm, normal (0,-1,0), area 10.1mm2, adj f158,f159,f160,f161,f162,f163,f164,f165
  f179: extruded ~0.36x0.32mm, area 0mm2, adj f27,f180,f186,f187
  f180: plane 0.05x0mm, normal (-1,0,0), area 0mm2, adj f27,f179,f181,f187
  f181: extruded ~0.38x0.33mm, area 0mm2, adj f27,f180,f182,f187
  f182: plane 0.1x0.05mm, normal (0,0,1), area 0mm2, adj f27,f181,f183,f187
  f183: plane 0.32x0.05mm, normal (-1,0,0), area 0mm2, adj f27,f182,f184,f187
  f184: plane 0.21x0.05mm, normal (0,0,1), area 0mm2, adj f27,f183,f185,f187
  f185: plane 0.97x0.05mm, normal (1,0,0), area 0mm2, adj f27,f184,f186,f187
  f186: plane 0.32x0.05mm, normal (0,0,-1), area 0mm2, adj f27,f179,f185,f187
  f187: plane 0.97x0.68mm, normal (0,-1,0), area 0.4mm2, adj f179,f180,f181,f182,f183,f184,f185,f186
  f188: extruded ~0.16x0.14mm, area 0mm2, adj f187,f189,f193,f274
  f189: plane 0.1x0.05mm, normal (0,0,-1), area 0mm2, adj f187,f188,f190,f274
  f190: plane 0.28x0.05mm, normal (-1,0,0), area 0mm2, adj f187,f189,f191,f274
  f191: plane 0.1x0.05mm, normal (0,0,1), area 0mm2, adj f187,f190,f192,f274
  f192: extruded ~0.17x0.14mm, area 0mm2, adj f187,f191,f193,f274
  f193: plane 0.05x0mm, normal (1,0,0), area 0mm2, adj f187,f188,f192,f274
  f194: plane 0.97x0.05mm, normal (1,0,0), area 0mm2, adj f27,f195,f197,f198
  f195: plane 0.2x0.05mm, normal (0,0,-1), area 0mm2, adj f27,f194,f196,f198
  f196: plane 0.97x0.05mm, normal (-1,0,0), area 0mm2, adj f27,f195,f197,f198
  f197: plane 0.2x0.05mm, normal (0,0,1), area 0mm2, adj f27,f194,f196,f198
  f198: plane 0.97x0.2mm, normal (0,-1,0), area 0.2mm2, adj f194,f195,f196,f197
  f199: extruded ~0.13x0.11mm, area 0mm2, adj f27,f200,f202,f203
  f200: extruded ~0.13x0.11mm, area 0mm2, adj f27,f199,f201,f203
  f201: extruded ~0.13x0.11mm, area 0mm2, adj f27,f200,f202,f203
  f202: extruded ~0.13x0.11mm, area 0mm2, adj f27,f199,f201,f203
  f203: plane 0.26x0.22mm, normal (0,-1,0), area 0mm2, adj f199,f200,f201,f202,f204,f205,f206,f207
  f204: extruded ~0.09x0.07mm, area 0mm2, adj f203,f205,f207,f275
  f205: extruded ~0.09x0.07mm, area 0mm2, adj f203,f204,f206,f275
  f206: extruded ~0.09x0.07mm, area 0mm2, adj f203,f205,f207,f275
  f207: extruded ~0.09x0.07mm, area 0mm2, adj f203,f204,f206,f275
  f208: plane 0.05x0.05mm, normal (-1,0,0), area 0mm2, adj f27,f209,f221,f222
  f209: extruded ~0.08x0.05mm, area 0mm2, adj f27,f208,f210,f222
  f210: extruded ~0.08x0.05mm, area 0mm2, adj f27,f209,f211,f222
  f211: extruded ~0.1x0.05mm, area 0mm2, adj f27,f210,f212,f222
  f212: extruded ~0.13x0.12mm, area 0mm2, adj f27,f211,f213,f222
  f213: extruded ~0.08x0.05mm, area 0mm2, adj f27,f212,f214,f222
  f214: plane 0.05x0.05mm, normal (-1,0,0), area 0mm2, adj f27,f213,f215,f222
  f215: plane 0.05x0mm, normal (0,0,1), area 0mm2, adj f27,f214,f216,f222
  f216: extruded ~0.08x0.05mm, area 0mm2, adj f27,f215,f217,f222
  f217: extruded ~0.09x0.07mm, area 0mm2, adj f27,f216,f218,f222
  f218: extruded ~0.09x0.07mm, area 0mm2, adj f27,f217,f219,f222
  f219: cylinder r=0.1mm len=0.05mm, axis (0,-1,0), area 0mm2, adj f27,f218,f220,f222
  f220: cylinder r=0.17mm len=0.05mm, axis (0,-1,0), area 0mm2, adj f27,f219,f221,f222
  f221: plane 0.05x0mm, normal (0,0,-1), area 0mm2, adj f27,f208,f220,f222
  f222: plane 0.25x0.19mm, normal (0,-1,0), area 0mm2, adj f208,f209,f210,f211,f212,f213,f214,f215
  f223: extruded ~0.33x0.32mm, area 0mm2, adj f27,f224,f228,f229
  f224: plane 0.05x0mm, normal (1,0,0), area 0mm2, adj f27,f223,f225,f229
  f225: extruded ~0.33x0.32mm, area 0mm2, adj f27,f224,f226,f229
  f226: extruded ~0.33x0.32mm, area 0mm2, adj f27,f225,f227,f229
  f227: plane 0.05x0mm, normal (-1,0,0), area 0mm2, adj f27,f226,f228,f229
  f228: extruded ~0.33x0.32mm, area 0mm2, adj f27,f223,f227,f229
  f229: plane 0.66x0.64mm, normal (0,-1,0), area 0.3mm2, adj f223,f224,f225,f226,f227,f228,f230,f231
  f230: extruded ~0.15x0.14mm, area 0mm2, adj f229,f231,f235,f276
  f231: extruded ~0.15x0.14mm, area 0mm2, adj f229,f230,f232,f276
  f232: plane 0.05x0mm, normal (-1,0,0), area 0mm2, adj f229,f231,f233,f276
  f233: extruded ~0.15x0.14mm, area 0mm2, adj f229,f232,f234,f276
  f234: extruded ~0.15x0.14mm, area 0mm2, adj f229,f233,f235,f276
  f235: plane 0.05x0mm, normal (1,0,0), area 0mm2, adj f229,f230,f234,f276
  f236: extruded ~0.29x0.29mm, area 0mm2, adj f27,f237,f245,f246
  f237: plane 0.35x0.05mm, normal (1,0,0), area 0mm2, adj f27,f236,f238,f246
  f238: plane 0.2x0.05mm, normal (0,0,-1), area 0mm2, adj f27,f237,f239,f246
  f239: plane 0.36x0.05mm, normal (-1,0,0), area 0mm2, adj f27,f238,f240,f246
  f240: extruded ~0.11x0.09mm, area 0mm2, adj f27,f239,f241,f246
  f241: extruded ~0.1x0.09mm, area 0mm2, adj f27,f240,f242,f246
  f242: plane 0.36x0.05mm, normal (1,0,0), area 0mm2, adj f27,f241,f243,f246
  f243: plane 0.2x0.05mm, normal (0,0,-1), area 0mm2, adj f27,f242,f244,f246
  f244: plane 0.35x0.05mm, normal (-1,0,0), area 0mm2, adj f27,f243,f245,f246
  f245: extruded ~0.29x0.29mm, area 0mm2, adj f27,f236,f244,f246
  f246: plane 0.64x0.58mm, normal (0,-1,0), area 0.3mm2, adj f236,f237,f238,f239,f240,f241,f242,f243
  f247: plane 0.16x0.05mm, normal (-1,0,0), area 0mm2, adj f27,f248,f268,f269
  f248: plane 0.05x0.04mm, normal (0,0,1), area 0mm2, adj f27,f247,f249,f269
  f249: plane 0.14x0.05mm, normal (1,0,0), area 0mm2, adj f27,f248,f250,f269
  f250: extruded ~0.05x0.05mm, area 0mm2, adj f27,f249,f251,f269
  f251: extruded ~0.05x0.04mm, area 0mm2, adj f27,f250,f252,f269
  f252: extruded ~0.07x0.05mm, area 0mm2, adj f27,f251,f253,f269
  f253: cylinder r=0.2mm len=0.05mm, axis (0,1,0), area 0mm2, adj f27,f252,f254,f269
  f254: plane 0.16x0.05mm, normal (-1,0,0), area 0mm2, adj f27,f253,f255,f269
  f255: plane 0.05x0.04mm, normal (0,0,1), area 0mm2, adj f27,f254,f256,f269
  f256: plane 0.14x0.05mm, normal (1,0,0), area 0mm2, adj f27,f255,f257,f269
  f257: extruded ~0.05x0.05mm, area 0mm2, adj f27,f256,f258,f269
  f258: extruded ~0.05x0.04mm, area 0mm2, adj f27,f257,f259,f269
  f259: extruded ~0.07x0.05mm, area 0mm2, adj f27,f258,f260,f269
  f260: plane 0.18x0.05mm, normal (-1,0,0), area 0mm2, adj f27,f259,f261,f269
  f261: plane 0.05x0.04mm, normal (0,0,1), area 0mm2, adj f27,f260,f262,f269
  f262: plane 0.24x0.05mm, normal (1,0,0), area 0mm2, adj f27,f261,f263,f269
  f263: plane 0.05x0.04mm, normal (0,0,-1), area 0mm2, adj f27,f262,f264,f269
  f264: plane 0.05x0.03mm, normal (-1,0,0), area 0mm2, adj f27,f263,f265,f269
  f265: extruded ~0.08x0.05mm, area 0mm2, adj f27,f264,f266,f269
  f266: cylinder r=0.07mm len=0.07mm, axis (0,1,0), area 0mm2, adj f27,f265,f267,f269
  f267: extruded ~0.09x0.05mm, area 0mm2, adj f27,f266,f268,f269
  f268: extruded ~0.09x0.08mm, area 0mm2, adj f27,f247,f267,f269
  f269: plane 0.35x0.25mm, normal (0,-1,0), area 0mm2, adj f247,f248,f249,f250,f251,f252,f253,f254
  f270: plane 0.18x0.14mm, normal (0,-1,0), area 0mm2, adj f49,f50,f51,f52
  f271: plane 0.18x0.14mm, normal (0,-1,0), area 0mm2, adj f92,f93,f94,f95
  f272: plane 0.18x0.13mm, normal (0,-1,0), area 0mm2, adj f107,f108,f109,f110,f111
  f273: plane 0.3x0.29mm, normal (0,-1,0), area 0.1mm2, adj f147,f148,f149,f150,f151,f152
  f274: plane 0.28x0.26mm, normal (0,-1,0), area 0.1mm2, adj f188,f189,f190,f191,f192,f193
  f275: plane 0.18x0.14mm, normal (0,-1,0), area 0mm2, adj f204,f205,f206,f207
  f276: plane 0.3x0.28mm, normal (0,-1,0), area 0.1mm2, adj f230,f231,f232,f233,f234,f235
PLACE A rot(axis=(-0.58,0.58,0.58),120deg) t=(-36.32,8.83,27.37)mm
PLACE B rot(axis=(1,0,0),180deg) t=(-36.32,-10.67,27.37)mm fixed
MATE cylindrical A.f65 <-> B.f9  axis (0,-1,0) through (-36.32,-14.67,17.85)mm
